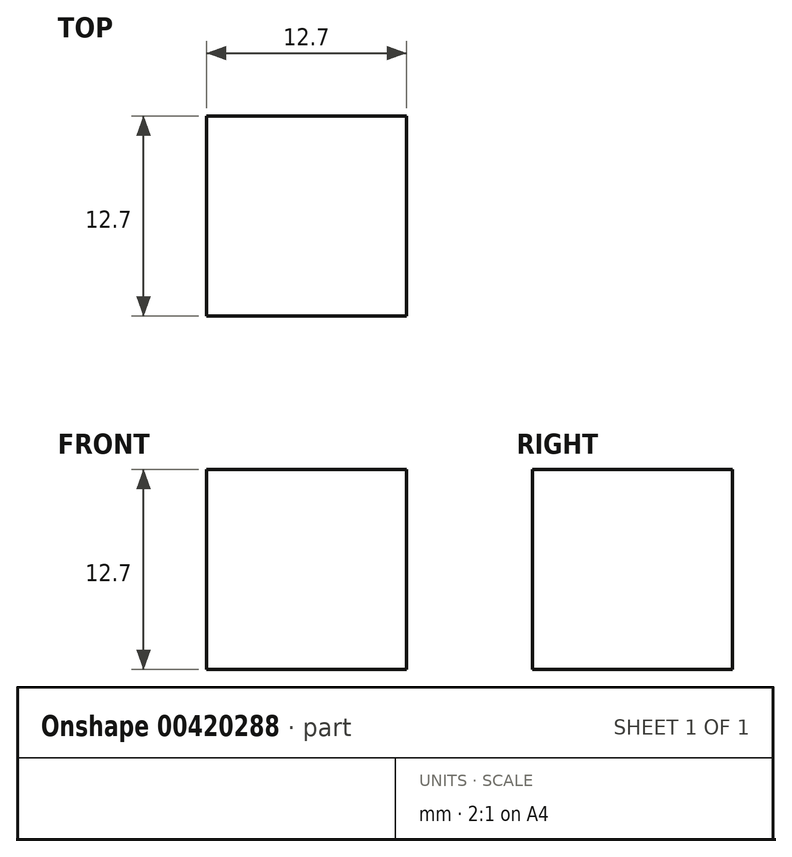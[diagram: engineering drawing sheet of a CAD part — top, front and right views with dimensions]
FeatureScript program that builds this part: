
annotation { "Feature Type Name" : "Feature", "Feature Type Description" : "" }
export const myFeature = defineFeature(function(context is Context, id is Id, definition is map)
    precondition{}
    {
        {
            var Q0;
            Q0=qCreatedBy(makeId("Top.planeOp"),FACE);
            var sketch = newSketch(context, id + "F0", { "sketchPlane" : qUnion([Q0])});
            skLineSegment(sketch, "E0.bottom", {"start": v(6.35, 6.35) * mm, "end": v(-6.35, 6.35) * mm});
            skLineSegment(sketch, "E0.top", {"start": v(6.35, -6.35) * mm, "end": v(-6.35, -6.35) * mm});
            skLineSegment(sketch, "E0.left", {"start": v(6.35, 6.35) * mm, "end": v(6.35, -6.35) * mm});
            skLineSegment(sketch, "E0.right", {"start": v(-6.35, 6.35) * mm, "end": v(-6.35, -6.35) * mm});
            skPoint(sketch, "E0.middle", {"position": v(0, 0) * mm});
            skSolve(sketch);
        }
        {
            var Q0;
            Q0=makeQuery(id+"F0.imprint","IMPRINT",FACE,{"disambiguationData":[TD([[makeQuery(id+"F0.imprint","IMPRINT",EDGE,{"derivedFrom":sQuery(id+"F0.wireOp",EDGE,"E0.bottom")}),1.0]])]});
            extrude(context, id + "F1", {"entities" : qUnion([Q0]), "depth" : 12.7 * mm});
        }
    });
